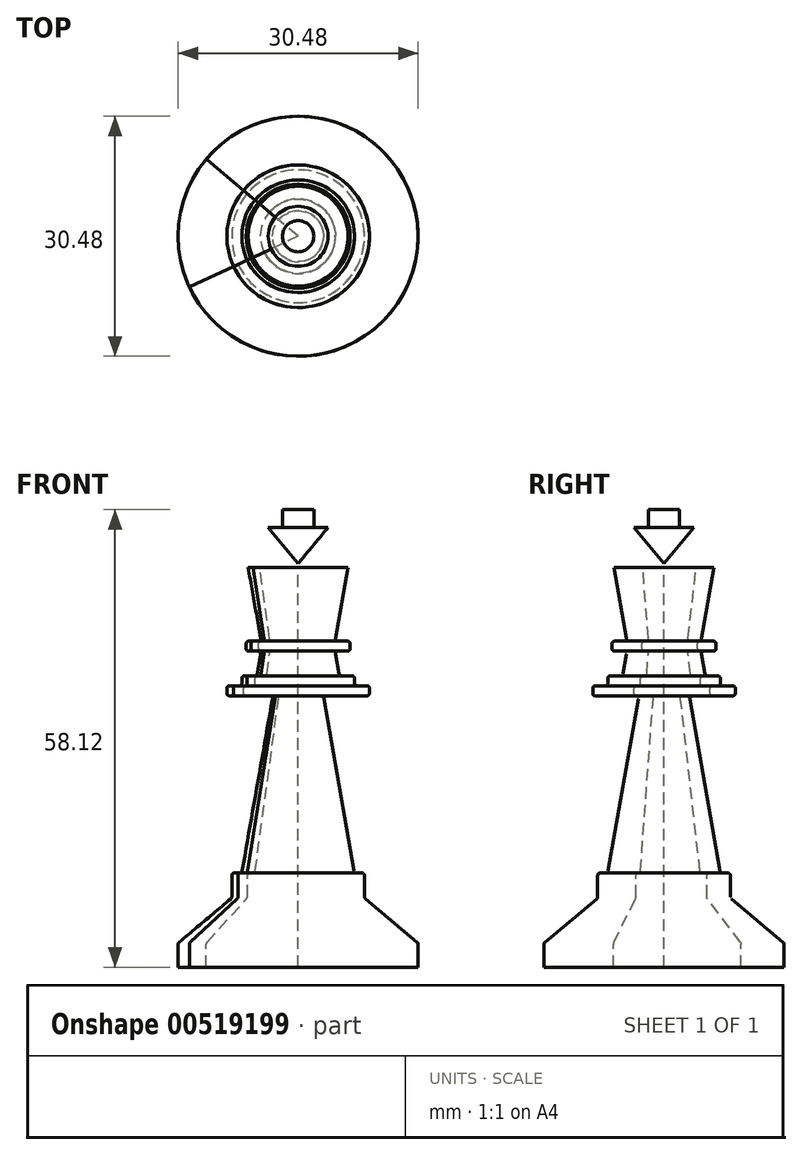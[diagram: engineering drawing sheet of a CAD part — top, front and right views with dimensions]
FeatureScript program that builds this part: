
annotation { "Feature Type Name" : "Feature", "Feature Type Description" : "" }
export const myFeature = defineFeature(function(context is Context, id is Id, definition is map)
    precondition{}
    {
        {
            var Q0;
            Q0=qCreatedBy(makeId("Front.planeOp"),FACE);
            var sketch = newSketch(context, id + "F0", { "sketchPlane" : qUnion([Q0])});
            skLineSegment(sketch, "E0.bottom", {"start": v(0, 0) * mm, "end": v(-15.24, 0) * mm});
            skLineSegment(sketch, "E0.top", {"start": v(0, 50.8) * mm, "end": v(-6.35, 50.8) * mm});
            skLineSegment(sketch, "E0.left", {"start": v(0, 0) * mm, "end": v(0, 50.8) * mm});
            skLineSegment(sketch, "E1", {"start": v(-15.24, 0) * mm, "end": v(-15.24, 2.93) * mm});
            skLineSegment(sketch, "E2", {"start": v(-15.13, 3.18) * mm, "end": v(-8.54, 8.7) * mm});
            skLineSegment(sketch, "E3", {"start": v(-8.43, 8.94) * mm, "end": v(-8.43, 11.65) * mm});
            skLineSegment(sketch, "E4", {"start": v(-8.11, 11.97) * mm, "end": v(-7.43, 11.97) * mm});
            skLineSegment(sketch, "E5", {"start": v(-7.11, 12.23) * mm, "end": v(-3.26, 34.11) * mm});
            skLineSegment(sketch, "E6", {"start": v(-3.57, 34.48) * mm, "end": v(-8.74, 34.48) * mm});
            skLineSegment(sketch, "E7", {"start": v(-9.06, 34.8) * mm, "end": v(-9.06, 35.44) * mm});
            skLineSegment(sketch, "E8", {"start": v(-8.74, 35.75) * mm, "end": v(-7.47, 35.75) * mm});
            skLineSegment(sketch, "E9", {"start": v(-7.15, 36.07) * mm, "end": v(-7.15, 36.7) * mm});
            skLineSegment(sketch, "E10", {"start": v(-6.83, 37.02) * mm, "end": v(-5.51, 37.02) * mm});
            skLineSegment(sketch, "E11", {"start": v(-5.2, 37.29) * mm, "end": v(-4.76, 39.78) * mm});
            skLineSegment(sketch, "E12", {"start": v(-5.07, 40.15) * mm, "end": v(-6.28, 40.15) * mm});
            skLineSegment(sketch, "E13", {"start": v(-6.6, 40.47) * mm, "end": v(-6.6, 41.1) * mm});
            skLineSegment(sketch, "E14", {"start": v(-6.28, 41.42) * mm, "end": v(-5.07, 41.42) * mm});
            skLineSegment(sketch, "E15", {"start": v(-4.76, 41.8) * mm, "end": v(-6.35, 50.8) * mm});
            skPoint(sketch, "E16.visualSharp", {"position": v(-15.24, 3.08) * mm});
            skArc(sketch, "E16.filletArc", {"start": v(-15.13, 3.18) * mm, "mid": v(-15.21, 3.07) * mm, "end": v(-15.24, 2.93) * mm});
            skPoint(sketch, "E17.visualSharp", {"position": v(-8.43, 8.8) * mm});
            skArc(sketch, "E17.filletArc", {"start": v(-8.54, 8.7) * mm, "mid": v(-8.46, 8.8) * mm, "end": v(-8.43, 8.94) * mm});
            skPoint(sketch, "E18.visualSharp", {"position": v(-3.2, 34.48) * mm});
            skArc(sketch, "E18.filletArc", {"start": v(-3.26, 34.11) * mm, "mid": v(-3.33, 34.37) * mm, "end": v(-3.57, 34.48) * mm});
            skPoint(sketch, "E19.visualSharp", {"position": v(-8.43, 11.97) * mm});
            skArc(sketch, "E19.filletArc", {"start": v(-8.11, 11.97) * mm, "mid": v(-8.34, 11.88) * mm, "end": v(-8.43, 11.65) * mm});
            skPoint(sketch, "E20.visualSharp", {"position": v(-7.16, 11.97) * mm});
            skArc(sketch, "E20.filletArc", {"start": v(-7.43, 11.97) * mm, "mid": v(-7.22, 12.04) * mm, "end": v(-7.11, 12.23) * mm});
            skPoint(sketch, "E21.visualSharp", {"position": v(-9.06, 34.48) * mm});
            skArc(sketch, "E21.filletArc", {"start": v(-9.06, 34.8) * mm, "mid": v(-8.96, 34.58) * mm, "end": v(-8.74, 34.48) * mm});
            skPoint(sketch, "E22.visualSharp", {"position": v(-9.06, 35.75) * mm});
            skArc(sketch, "E22.filletArc", {"start": v(-8.74, 35.75) * mm, "mid": v(-8.96, 35.66) * mm, "end": v(-9.06, 35.44) * mm});
            skPoint(sketch, "E23.visualSharp", {"position": v(-7.15, 35.75) * mm});
            skArc(sketch, "E23.filletArc", {"start": v(-7.47, 35.75) * mm, "mid": v(-7.25, 35.85) * mm, "end": v(-7.15, 36.07) * mm});
            skPoint(sketch, "E24.visualSharp", {"position": v(-7.15, 37.02) * mm});
            skArc(sketch, "E24.filletArc", {"start": v(-6.83, 37.02) * mm, "mid": v(-7.06, 36.93) * mm, "end": v(-7.15, 36.7) * mm});
            skPoint(sketch, "E25.visualSharp", {"position": v(-5.25, 37.02) * mm});
            skArc(sketch, "E25.filletArc", {"start": v(-5.51, 37.02) * mm, "mid": v(-5.3, 37.1) * mm, "end": v(-5.2, 37.29) * mm});
            skPoint(sketch, "E26.visualSharp", {"position": v(-4.7, 40.15) * mm});
            skArc(sketch, "E26.filletArc", {"start": v(-4.76, 39.78) * mm, "mid": v(-4.83, 40.04) * mm, "end": v(-5.07, 40.15) * mm});
            skPoint(sketch, "E27.visualSharp", {"position": v(-6.6, 40.15) * mm});
            skArc(sketch, "E27.filletArc", {"start": v(-6.6, 40.47) * mm, "mid": v(-6.5, 40.24) * mm, "end": v(-6.28, 40.15) * mm});
            skPoint(sketch, "E28.visualSharp", {"position": v(-6.6, 41.42) * mm});
            skArc(sketch, "E28.filletArc", {"start": v(-6.28, 41.42) * mm, "mid": v(-6.5, 41.33) * mm, "end": v(-6.6, 41.1) * mm});
            skPoint(sketch, "E29.visualSharp", {"position": v(-4.7, 41.42) * mm});
            skArc(sketch, "E29.filletArc", {"start": v(-5.07, 41.42) * mm, "mid": v(-4.83, 41.53) * mm, "end": v(-4.76, 41.8) * mm});
            skSolve(sketch);
        }
        {
            var Q0;
            Q0=makeQuery(id+"F0.imprint","IMPRINT",FACE,{"disambiguationData":[TD([[makeQuery(id+"F0.imprint","IMPRINT",EDGE,{"derivedFrom":sQuery(id+"F0.wireOp",EDGE,"E0.bottom")}),-1.0]])]});
            var Q1;
            Q1=sQuery(id+"F0.wireOp",EDGE,"E0.left");
            revolve(context, id + "F1", {"entities" : qUnion([Q0]), "axis" : qUnion([Q1]), "revolveType" : RevolveType.TWO_DIRECTIONS, "angle" : 320 * degree, "angleBack" : 25 * degree});
        }
        {
            var Q0;
            Q0=qCreatedBy(makeId("Right.planeOp"),FACE);
            var sketch = newSketch(context, id + "F2", { "sketchPlane" : qUnion([Q0])});
            skLineSegment(sketch, "E30", {"start": v(0, 51.28) * mm, "end": v(-3.8, 55.88) * mm});
            skLineSegment(sketch, "E31", {"start": v(-3.8, 55.88) * mm, "end": v(0, 55.88) * mm});
            skLineSegment(sketch, "E32", {"start": v(0, 58.12) * mm, "end": v(-1.98, 58.12) * mm});
            skLineSegment(sketch, "E33", {"start": v(-1.98, 58.12) * mm, "end": v(-1.98, 55.88) * mm});
            skLineSegment(sketch, "E34", {"start": v(-1.98, 55.88) * mm, "end": v(0, 55.88) * mm});
            skLineSegment(sketch, "E35", {"start": v(0, 51.28) * mm, "end": v(0, 55.88) * mm});
            skLineSegment(sketch, "E36", {"start": v(0, 55.88) * mm, "end": v(0, 58.12) * mm});
            skSolve(sketch);
        }
        {
            var Q0;
            Q0=makeQuery(id+"F2.imprint","IMPRINT",FACE,{"disambiguationData":[TD([[makeQuery(id+"F2.imprint","IMPRINT",EDGE,{"derivedFrom":sQuery(id+"F2.wireOp",EDGE,"E30")}),-1.0]])]});
            var Q1;
            Q1=makeQuery(id+"F2.imprint","IMPRINT",FACE,{"disambiguationData":[TD([[makeQuery(id+"F2.imprint","IMPRINT",EDGE,{"derivedFrom":sQuery(id+"F2.wireOp",EDGE,"E32")}),1.0]])]});
            var Q2;
            Q2=sQuery(id+"F2.wireOp",EDGE,"E36");
            revolve(context, id + "F3", {"entities" : qUnion([Q0, Q1]), "axis" : qUnion([Q2]), "revolveType" : RevolveType.FULL});
        }
        {
            var Q0;
            Q0=makeQuery(id+"F0.imprint","IMPRINT",FACE,{"disambiguationData":[TD([[makeQuery(id+"F0.imprint","IMPRINT",EDGE,{"derivedFrom":sQuery(id+"F0.wireOp",EDGE,"E0.bottom")}),-1.0]])]});
            var Q1;
            Q1=sQuery(id+"F0.wireOp",EDGE,"E0.left");
            revolve(context, id + "F4", {"entities" : qUnion([Q0]), "axis" : qUnion([Q1]), "revolveType" : RevolveType.FULL});
        }
    });
